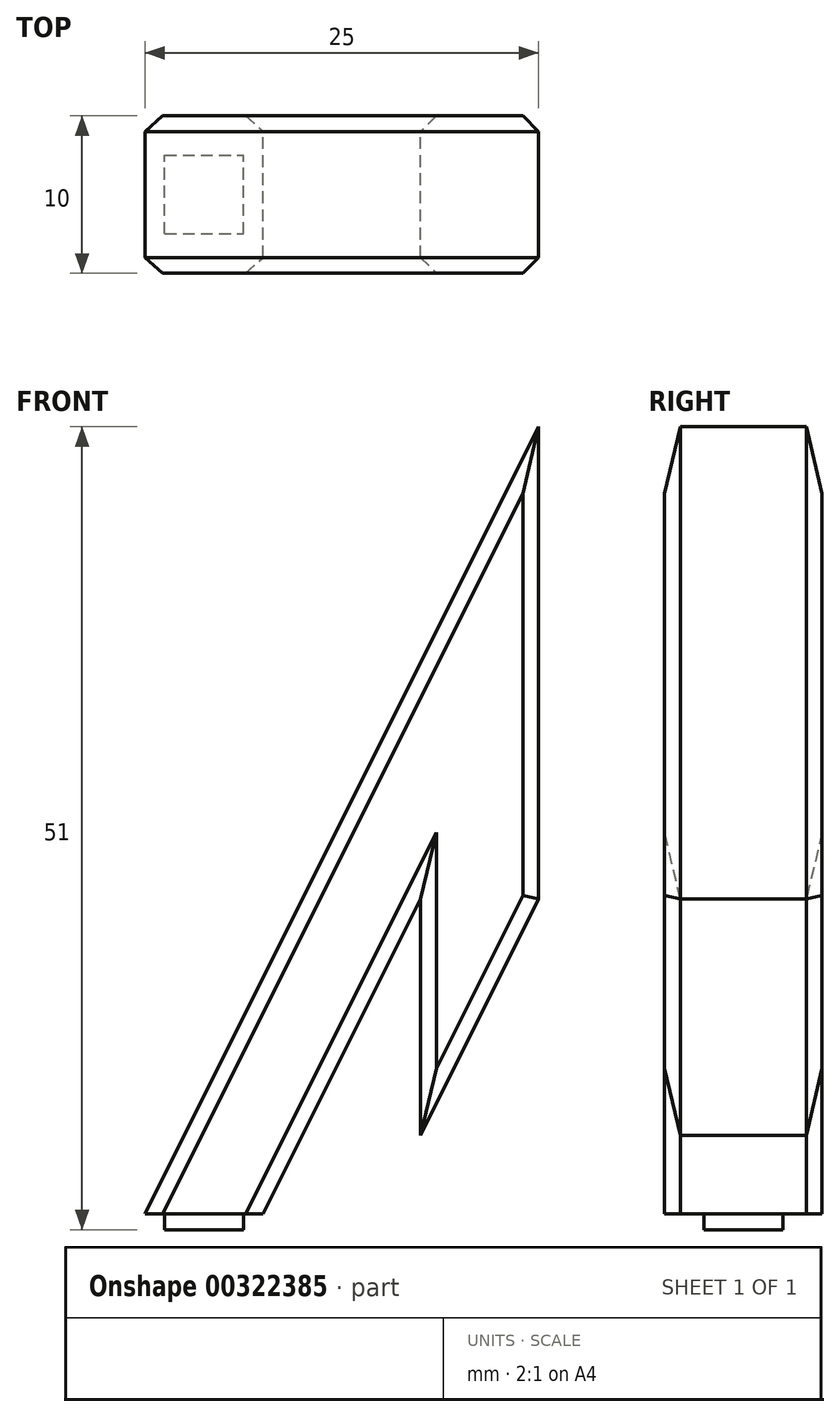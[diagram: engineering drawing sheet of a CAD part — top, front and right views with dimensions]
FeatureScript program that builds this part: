
annotation { "Feature Type Name" : "Feature", "Feature Type Description" : "" }
export const myFeature = defineFeature(function(context is Context, id is Id, definition is map)
    precondition{}
    {
        {
            var Q0;
            Q0=qCreatedBy(makeId("Front.planeOp"),FACE);
            var sketch = newSketch(context, id + "F0", { "sketchPlane" : qUnion([Q0])});
            skLineSegment(sketch, "E0", {"start": v(0, 50) * mm, "end": v(-25, 0) * mm});
            skLineSegment(sketch, "E1", {"start": v(-25, 0) * mm, "end": v(0, 0) * mm});
            skLineSegment(sketch, "E2", {"start": v(0, 0) * mm, "end": v(0, 50) * mm});
            skLineSegment(sketch, "E3", {"start": v(-7.5, 20) * mm, "end": v(-17.5, 0) * mm});
            skLineSegment(sketch, "E4", {"start": v(-17.5, 0) * mm, "end": v(-7.5, 0) * mm});
            skLineSegment(sketch, "E5", {"start": v(-7.5, 0) * mm, "end": v(-7.5, 20) * mm});
            skLineSegment(sketch, "E6", {"start": v(0, 20) * mm, "end": v(-7.5, 5) * mm});
            skSolve(sketch);
        }
        {
            var Q0;
            {var subQ1=sQuery(id+"F0.wireOp",EDGE,"E0");Q0=makeQuery(id+"F0.imprint","IMPRINT",FACE,{"disambiguationData":[TD([[makeQuery(id+"F0.imprint","IMPRINT",EDGE,{"derivedFrom":subQ1}),1.0]])]});}
            extrude(context, id + "F1", {"entities" : qUnion([Q0]), "depth" : 10 * mm});
        }
        {
            var Q0;
            Q0=makeQuery(id+"F1.opExtrude","SWEPT_FACE",FACE,{"disambiguationData":[OSD([sQuery(id+"F0.wireOp",EDGE,"E1")])]});
            var sketch = newSketch(context, id + "F2", { "sketchPlane" : qUnion([Q0])});
            skLineSegment(sketch, "E7.bottom", {"start": v(-23.75, 7.5) * mm, "end": v(-18.75, 7.5) * mm});
            skLineSegment(sketch, "E7.top", {"start": v(-23.75, 2.5) * mm, "end": v(-18.75, 2.5) * mm});
            skLineSegment(sketch, "E7.left", {"start": v(-23.75, 7.5) * mm, "end": v(-23.75, 2.5) * mm});
            skLineSegment(sketch, "E7.right", {"start": v(-18.75, 7.5) * mm, "end": v(-18.75, 2.5) * mm});
            skLineSegment(sketch, "E8", {"start": v(-21.25, 7.5) * mm, "end": v(-21.25, 10) * mm});
            skLineSegment(sketch, "E9", {"start": v(-18.75, 5) * mm, "end": v(-17.5, 5) * mm});
            skLineSegment(sketch, "E10", {"start": v(-21.25, 2.5) * mm, "end": v(-21.25, 0) * mm});
            skLineSegment(sketch, "E11", {"start": v(-23.75, 5) * mm, "end": v(-25, 5) * mm});
            skSolve(sketch);
        }
        {
            var Q0;
            {var subQ4=sQuery(id+"F2.wireOp",EDGE,"E7.left");var subQ6=sQuery(id+"F2.wireOp",EDGE,"E7.bottom");var subQ9=makeQuery(id+"F2.imprint","INTERSECT",VERTEX,{"derivedFrom":[subQ6,subQ4]});Q0=makeQuery(id+"F2.imprint","IMPRINT",FACE,{"disambiguationData":[TD([[makeQuery(id+"F2.imprint","IMPRINT",EDGE,{"disambiguationData":[TD([[subQ9,-1.0]])],"derivedFrom":subQ6}),-1.0]])]});}
            extrude(context, id + "F3", {"entities" : qUnion([Q0]), "operationType" : NewBodyOperationType.ADD, "depth" : 1 * mm});
        }
        {
            var Q0;
            Q0=makeQuery(id+"F1.opExtrude","CAP_EDGE",EDGE,{"disambiguationData":[OSD([sQuery(id+"F0.wireOp",EDGE,"E0")])],"isStart":false});
            var Q1;
            Q1=makeQuery(id+"F1.opExtrude","CAP_EDGE",EDGE,{"disambiguationData":[OSD([sQuery(id+"F0.wireOp",EDGE,"E2")])],"isStart":false});
            var Q2;
            Q2=makeQuery(id+"F1.opExtrude","CAP_EDGE",EDGE,{"disambiguationData":[OSD([sQuery(id+"F0.wireOp",EDGE,"E0")])],"isStart":true});
            var Q3;
            Q3=makeQuery(id+"F1.opExtrude","CAP_EDGE",EDGE,{"disambiguationData":[OSD([sQuery(id+"F0.wireOp",EDGE,"E2")])],"isStart":true});
            var Q4;
            Q4=makeQuery(id+"F1.opExtrude","CAP_EDGE",EDGE,{"disambiguationData":[OSD([sQuery(id+"F0.wireOp",EDGE,"E3")])],"isStart":false});
            var Q5;
            Q5=makeQuery(id+"F1.opExtrude","CAP_EDGE",EDGE,{"disambiguationData":[OSD([sQuery(id+"F0.wireOp",EDGE,"E5")])],"isStart":false});
            var Q6;
            Q6=makeQuery(id+"F1.opExtrude","CAP_EDGE",EDGE,{"disambiguationData":[OSD([sQuery(id+"F0.wireOp",EDGE,"E3")])],"isStart":true});
            var Q7;
            Q7=makeQuery(id+"F1.opExtrude","CAP_EDGE",EDGE,{"disambiguationData":[OSD([sQuery(id+"F0.wireOp",EDGE,"E5")])],"isStart":true});
            var Q8;
            Q8=makeQuery(id+"F1.opExtrude","CAP_EDGE",EDGE,{"disambiguationData":[OSD([sQuery(id+"F0.wireOp",EDGE,"E6")])],"isStart":false});
            var Q9;
            Q9=makeQuery(id+"F1.opExtrude","CAP_EDGE",EDGE,{"disambiguationData":[OSD([sQuery(id+"F0.wireOp",EDGE,"E6")])],"isStart":true});
            chamfer(context, id + "F4", {"entities" : qUnion([Q0, Q1, Q2, Q3, Q4, Q5, Q6, Q7, Q8, Q9]), "width" : 1 * mm, "tangentPropagation" : true});
        }
    });
